# Revit family: RN 23121 Valvola di riempimento
name_source: partatom
category: Rohrzubehör
units: mm (PartAtom-declared; Revit-internal decimal feet)

## family parameters
Arbeitsebenenbasiert = Nein
Beim Laden mit Abzugskörper schneiden = Nein
Bemaßung runder Anschluss = Durchmesser verwenden
Gemeinsam genutzt = Nein
Immer vertikal = Ja
Teiletyp = Ventil - Zerlegung in

## types (1)
- DN 15
    1.010.00.2 Blattnummer der Richtlinie = 17
    1.010.00.3 Ausgabedatum (Monat) der Richtlinie = 201601
    1.010.00.4 Herstellername = R. Nussbaum AG
    1.010.00.5 Revisionsdatum der Datei = 20190528
    1.010.00.6 Webadresse des Herstellers = http://www.nussbaum.ch
    1.100.00.3 Sortiernummer für Anzeigereihenfolge = 1
    1.100.00.4 Produktbezeichnung = Absperrarmaturen
    1.800.00.3 TGA-Nummer = 0010640000000000000000000000020070000000000000000100000000
    1.810.00.3 Hersteller-Bestellnummer = 23121.04
    1.810.00.4 DATANORM-Nummer = 23121.04
    1.810.00.5 StLB-Nummer = 627.213
    1.810.00.6 GTIN-Nummer = 7612945737106
    1.960/3L.00.8 Link (URL) = https://www.nussbaum.ch
    17.700.00.30 Produktbeschreibung = 23121.04, Füllventil, mit Rückfl'verhind. EA/Schlauchverschr., DN=15, Rp=½
    17.700.00.4 Armaturentyp = 1
    17.700.00.5 Nennweite DN = 15
    17.700.00.6 kvs-Wert [m3/h] = 3.61
    17.700.00.7 Maximale Betriebstemperatur TB [°C] = 90
    17.700.00.8 Maximaler Betriebsdruck (Arbeitsdruck) ps [1.0 · 105 Pa] = 16
    CONNECTOR0_DIAMETER_dX_0r = 15 mm
    CONNECTOR0_dX_00 = 47 mm
    CONNECTOR0_dX_01 = 34 mm
    CONNECTOR0_ref_dX = 34 mm
    CONNECTOR1_DIAMETER_dX_0r = 10 mm  [stored 0.0328084 ft]
    CONNECTOR1_dX_00 = 26 mm
    CONNECTOR1_dX_01 = 55 mm
    CONNECTOR1_ref_dX = 26 mm
    Connector Visibility = Nein
    EnclosingSpace Visibility = Nein
    Hersteller = R. Nussbauzm AG
    Modell = 23121.04
    R. Nussbaum AG 23121.04 de Visibility = Ja
    Typenkommentare = Valvola di riempimentoDN 15
    URL = https://www.nussbaum.ch

note: [stored X ft] marks values corroborated as IEEE doubles in the binary element streams (Revit-internal decimal feet)

## geometry (parser evidence)
native form markers: Sweep x2
no freeform markers — native parametric forms only
